# Revit family: QF_ELECTROLUXPROFESSIONAL_206352_LIFT7E
name_source: partatom
category: Specialty Equipment
revit_build: Autodesk Revit 2018 (Build: 20190510_1515(x64)
units: mm (PartAtom-declared; Revit-internal decimal feet)

## family parameters
Always vertical = Yes
Cut with Voids When Loaded = No
Part Type = Normal
Room Calculation Point = No
Round Connector Dimension = Use Diameter
Shared = No
Work Plane-Based = No

## types (1)
- QF_ELECTROLUXPROFESSIONAL_206352_LIFT7E
    Apparent Power = 200 VA
    Conn Conduit = Yes
    Depth = 730 mm  [stored 2.39501 ft]
    Description = 700XP Automatic Basket Lifting System - 200 mm
    Direct Waste Size = 0"
    FL Amps = 1 A
    HP = 0.3 HP
    Height = 850 mm  [stored 2.78871 ft]
    Manufacturer = ELECTROLUX
    Max Overcurrent Protection = 0 A
    Min Ckt Ampacity = 0 A
    Model = 206352
    Phase = 1
    URL = www.electrolux.com
    URL Cutsheet = www.electrolux.com
    Volts = 230 V
    Watts = 200 W
    Weight in Pounds = 66
    Width = 200 mm  [stored 0.656168 ft]

note: [stored X ft] marks values corroborated as IEEE doubles in the binary element streams (Revit-internal decimal feet)

## geometry (parser evidence)
native form markers: Blend x24, Sweep x2
no freeform markers — native parametric forms only
